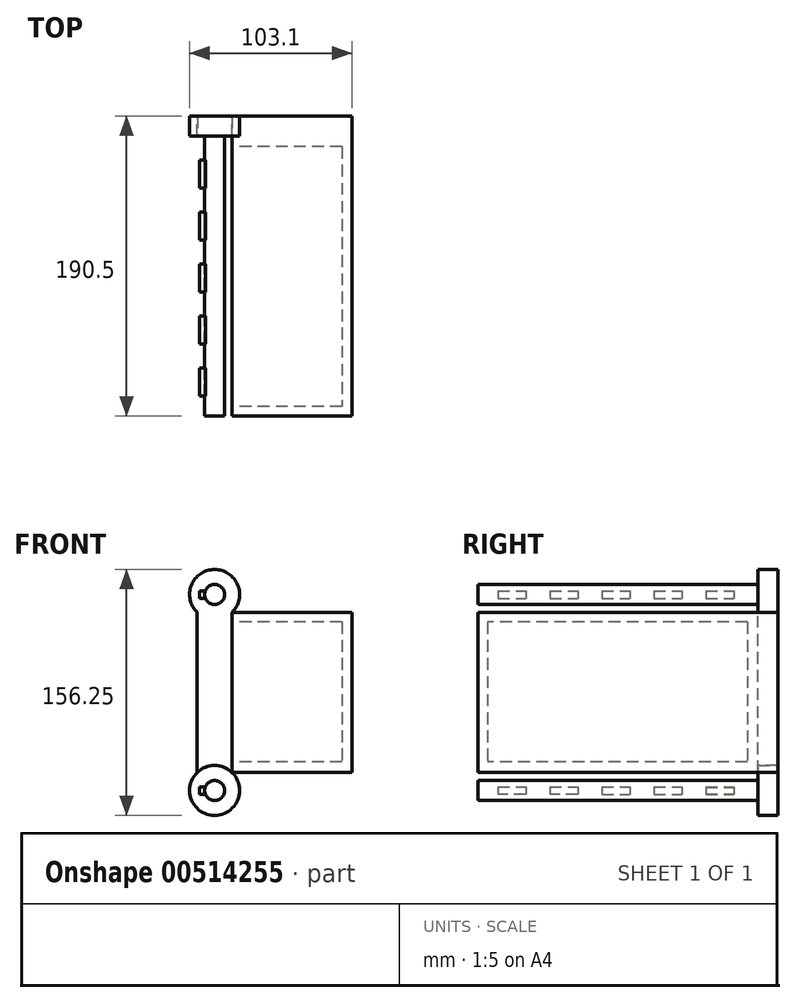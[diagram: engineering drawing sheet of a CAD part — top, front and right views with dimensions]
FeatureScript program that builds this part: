
annotation { "Feature Type Name" : "Feature", "Feature Type Description" : "" }
export const myFeature = defineFeature(function(context is Context, id is Id, definition is map)
    precondition{}
    {
        {
            var Q0;
            Q0=qCreatedBy(makeId("Front.planeOp"),FACE);
            var sketch = newSketch(context, id + "F0", { "sketchPlane" : qUnion([Q0])});
            skCircle(sketch, "E0", {"center": v(0, 0) * mm, "radius": 6.35 * mm});
            skSolve(sketch);
        }
        {
            var Q0;
            Q0=makeQuery(id+"F0.imprint","IMPRINT",FACE,{"disambiguationData":[TD([[makeQuery(id+"F0.imprint","IMPRINT",EDGE,{"derivedFrom":sQuery(id+"F0.wireOp",EDGE,"E0")}),1.0]])]});
            extrude(context, id + "F1", {"entities" : qUnion([Q0]), "depth" : 177.8 * mm, "offsetDistance" : 25.4 * mm});
        }
        {
            var Q0;
            Q0=makeQuery(id+"F1.opExtrude","CAP_FACE",FACE,{"disambiguationData":[OSD([sQuery(id+"F0.wireOp",EDGE,"E0")])],"isStart":true});
            var sketch = newSketch(context, id + "F2", { "sketchPlane" : qUnion([Q0])});
            skCircle(sketch, "E1", {"center": v(0, 0) * mm, "radius": 15.88 * mm});
            skSolve(sketch);
        }
        {
            var Q0;
            Q0=makeQuery(id+"F2.imprint","IMPRINT",FACE,{"disambiguationData":[TD([[makeQuery(id+"F2.imprint","IMPRINT",EDGE,{"derivedFrom":sQuery(id+"F2.wireOp",EDGE,"E1")}),1.0]])]});
            var Q1;
            Q1=makeQuery(id+"F2.imprint","IMPRINT",FACE,{"disambiguationData":[TD([[makeQuery(id+"F2.imprint","IMPRINT",EDGE,{"derivedFrom":makeQuery(id+"F1.opExtrude","CAP_EDGE",EDGE,{"disambiguationData":[OSD([sQuery(id+"F0.wireOp",EDGE,"E0")])],"isStart":true})}),-1.0]])]});
            extrude(context, id + "F3", {"entities" : qUnion([Q0, Q1]), "operationType" : NewBodyOperationType.ADD, "depth" : 12.7 * mm});
        }
        {
            var Q0;
            Q0=makeQuery(id+"F3.opExtrude","CAP_FACE",FACE,{"disambiguationData":[OSD([sQuery(id+"F2.wireOp",EDGE,"E1")])],"isStart":false});
            var sketch = newSketch(context, id + "F4", { "sketchPlane" : qUnion([Q0])});
            skArc(sketch, "E2", {"start": v(11, 11.44) * mm, "mid": v(0, 15.9) * mm, "end": v(-11.02, 11.43) * mm});
            skPoint(sketch, "E3.bottom.start.orphan", {"position": v(-15.88, 0) * mm});
            skLineSegment(sketch, "E4.bottom", {"start": v(-11.02, 11.43) * mm, "end": v(11, 11.43) * mm});
            skLineSegment(sketch, "E4.top", {"start": v(-11.02, 113.03) * mm, "end": v(11, 113.03) * mm});
            skLineSegment(sketch, "E4.left", {"start": v(-11.02, 11.43) * mm, "end": v(-11.02, 113.03) * mm});
            skLineSegment(sketch, "E4.right", {"start": v(11, 11.43) * mm, "end": v(11, 113.03) * mm});
            skLineSegment(sketch, "E5", {"start": v(0, 15.87) * mm, "end": v(0, 11.43) * mm});
            skPoint(sketch, "E5.startSnap0", {"position": v(0, 15.9) * mm});
            skPoint(sketch, "E5.endSnap0", {"position": v(0, 11.43) * mm});
            skSolve(sketch);
        }
        {
            var Q0;
            Q0=qCreatedBy(makeId("Front.planeOp"),FACE);
            var sketch = newSketch(context, id + "F5", { "sketchPlane" : qUnion([Q0])});
            skCircle(sketch, "E6", {"center": v(0, 124.5) * mm, "radius": 15.88 * mm});
            skSolve(sketch);
        }
        {
            var Q0;
            {var subQ0=sQuery(id+"F4.wireOp",EDGE,"E2");Q0=makeQuery(id+"F4.imprint","IMPRINT",FACE,{"disambiguationData":[TD([[makeQuery(id+"F4.imprint","IMPRINT",EDGE,{"derivedFrom":subQ0}),-1.0]])]});}
            extrude(context, id + "F6", {"entities" : qUnion([Q0]), "oppositeDirection" : true, "depth" : 12.7 * mm, "offsetDistance" : 25.4 * mm});
        }
        {
            var Q0;
            Q0=makeQuery(id+"F5.imprint","IMPRINT",FACE,{"disambiguationData":[TD([[makeQuery(id+"F5.imprint","IMPRINT",EDGE,{"derivedFrom":sQuery(id+"F5.wireOp",EDGE,"E6")}),1.0]])]});
            extrude(context, id + "F7", {"entities" : qUnion([Q0]), "operationType" : NewBodyOperationType.ADD, "oppositeDirection" : true, "depth" : 12.7 * mm, "offsetDistance" : 25.4 * mm});
        }
        {
            var Q0;
            Q0=makeQuery(id+"F7.boolean.opBoolean","MERGE",FACE,{"derivedFrom":[makeQuery(id+"F6.opExtrude","CAP_FACE",FACE,{"disambiguationData":[OSD([sQuery(id+"F4.wireOp",EDGE,"E2"),sQuery(id+"F4.wireOp",EDGE,"E4.top"),sQuery(id+"F4.wireOp",EDGE,"E4.left"),sQuery(id+"F4.wireOp",EDGE,"E4.right")])],"isStart":false}),makeQuery(id+"F7.opExtrude","CAP_FACE",FACE,{"disambiguationData":[OSD([sQuery(id+"F5.wireOp",EDGE,"E6")])],"isStart":true})]});
            var sketch = newSketch(context, id + "F8", { "sketchPlane" : qUnion([Q0])});
            skCircle(sketch, "E7", {"center": v(0, 124.5) * mm, "radius": 6.35 * mm});
            skSolve(sketch);
        }
        {
            var Q0;
            Q0=makeQuery(id+"F8.imprint","IMPRINT",FACE,{"disambiguationData":[TD([[makeQuery(id+"F8.imprint","IMPRINT",EDGE,{"derivedFrom":sQuery(id+"F8.wireOp",EDGE,"E7")}),1.0]])]});
            extrude(context, id + "F9", {"entities" : qUnion([Q0]), "operationType" : NewBodyOperationType.ADD, "depth" : 177.8 * mm, "offsetDistance" : 25.4 * mm});
        }
        {
            var Q0;
            Q0=makeQuery(id+"F7.boolean.opBoolean","MERGE",FACE,{"derivedFrom":[makeQuery(id+"F6.opExtrude","CAP_FACE",FACE,{"disambiguationData":[OSD([sQuery(id+"F4.wireOp",EDGE,"E2"),sQuery(id+"F4.wireOp",EDGE,"E4.top"),sQuery(id+"F4.wireOp",EDGE,"E4.left"),sQuery(id+"F4.wireOp",EDGE,"E4.right")])],"isStart":false}),makeQuery(id+"F7.opExtrude","CAP_FACE",FACE,{"disambiguationData":[OSD([sQuery(id+"F5.wireOp",EDGE,"E6")])],"isStart":true})]});
            var sketch = newSketch(context, id + "F10", { "sketchPlane" : qUnion([Q0])});
            skLineSegment(sketch, "E8.bottom", {"start": v(11.02, 113.03) * mm, "end": v(87.22, 113.03) * mm});
            skLineSegment(sketch, "E8.top", {"start": v(11.02, 11.43) * mm, "end": v(87.22, 11.43) * mm});
            skLineSegment(sketch, "E8.left", {"start": v(11.02, 113.03) * mm, "end": v(11.02, 11.43) * mm});
            skLineSegment(sketch, "E8.right", {"start": v(87.22, 113.03) * mm, "end": v(87.22, 11.43) * mm});
            skSolve(sketch);
        }
        {
            var Q0;
            Q0=makeQuery(id+"F10.imprint","IMPRINT",FACE,{"disambiguationData":[TD([[makeQuery(id+"F10.imprint","IMPRINT",EDGE,{"derivedFrom":sQuery(id+"F10.wireOp",EDGE,"E8.bottom")}),-1.0]])]});
            extrude(context, id + "F11", {"entities" : qUnion([Q0]), "operationType" : NewBodyOperationType.ADD, "depth" : 177.8 * mm, "offsetDistance" : 25.4 * mm, "hasSecondDirection" : true, "secondDirectionOppositeDirection" : true, "secondDirectionDepth" : 12.7 * mm});
        }
        {
            var Q0;
            Q0=makeQuery(id+"F11.opExtrude","SWEPT_FACE",FACE,{"disambiguationData":[OSD([sQuery(id+"F10.wireOp",EDGE,"E8.left")])]});
            var sketch = newSketch(context, id + "F12", { "sketchPlane" : qUnion([Q0])});
            skLineSegment(sketch, "E9.bottom", {"start": v(6.74, 107.06) * mm, "end": v(171.84, 107.06) * mm});
            skLineSegment(sketch, "E9.top", {"start": v(6.74, 18.16) * mm, "end": v(171.84, 18.16) * mm});
            skLineSegment(sketch, "E9.left", {"start": v(6.74, 107.06) * mm, "end": v(6.74, 18.16) * mm});
            skLineSegment(sketch, "E9.right", {"start": v(171.84, 107.06) * mm, "end": v(171.84, 18.16) * mm});
            skSolve(sketch);
        }
        {
            var Q0;
            Q0=makeQuery(id+"F12.imprint","IMPRINT",FACE,{"disambiguationData":[TD([[makeQuery(id+"F12.imprint","IMPRINT",EDGE,{"derivedFrom":sQuery(id+"F12.wireOp",EDGE,"E9.bottom")}),-1.0]])]});
            extrude(context, id + "F13", {"entities" : qUnion([Q0]), "operationType" : NewBodyOperationType.REMOVE, "oppositeDirection" : true, "depth" : 69.85 * mm, "offsetDistance" : 25.4 * mm});
        }
        {
            var Q0;
            Q0=makeQuery(id+"F3.opExtrude","CAP_FACE",FACE,{"disambiguationData":[OSD([sQuery(id+"F2.wireOp",EDGE,"E1")])],"isStart":true});
            var sketch = newSketch(context, id + "F14", { "sketchPlane" : qUnion([Q0])});
            skArc(sketch, "E10", {"start": v(-5.87, 2.41) * mm, "mid": v(-6.36, -0.03) * mm, "end": v(-5.85, -2.46) * mm});
            skLineSegment(sketch, "E11", {"start": v(-5.85, -2.46) * mm, "end": v(-9.66, -2.46) * mm});
            skLineSegment(sketch, "E12", {"start": v(-5.87, 2.41) * mm, "end": v(-9.68, 2.41) * mm});
            skLineSegment(sketch, "E13", {"start": v(-9.68, 2.41) * mm, "end": v(-9.66, -2.46) * mm});
            skSolve(sketch);
        }
        {
            var Q0;
            {var subQ0=sQuery(id+"F14.wireOp",EDGE,"E13");Q0=makeQuery(id+"F14.imprint","IMPRINT",FACE,{"disambiguationData":[TD([[makeQuery(id+"F14.imprint","IMPRINT",EDGE,{"derivedFrom":subQ0}),1.0]])]});}
            extrude(context, id + "F15", {"entities" : qUnion([Q0]), "operationType" : NewBodyOperationType.ADD, "depth" : 33.02 * mm, "offsetDistance" : 25.4 * mm, "hasSecondDirection" : true, "secondDirectionOppositeDirection" : false, "secondDirectionDepth" : 15.24 * mm});
        }
        {
            var Q0;
            Q0=makeQuery(id+"F15.opExtrude","CAP_FACE",FACE,{"disambiguationData":[OSD([sQuery(id+"F0.wireOp",EDGE,"E0"),sQuery(id+"F14.wireOp",EDGE,"E10"),sQuery(id+"F14.wireOp",EDGE,"E11"),sQuery(id+"F14.wireOp",EDGE,"E12"),sQuery(id+"F14.wireOp",EDGE,"E13")])],"isStart":false});
            var sketch = newSketch(context, id + "F16", { "sketchPlane" : qUnion([Q0])});
            skArc(sketch, "E14", {"start": v(-5.95, 2.41) * mm, "mid": v(-6.44, -0.02) * mm, "end": v(-5.93, -2.46) * mm});
            skLineSegment(sketch, "E15", {"start": v(-5.93, -2.46) * mm, "end": v(-9.74, -2.46) * mm});
            skLineSegment(sketch, "E16", {"start": v(-5.95, 2.41) * mm, "end": v(-9.76, 2.41) * mm});
            skLineSegment(sketch, "E17", {"start": v(-9.76, 2.41) * mm, "end": v(-9.74, -2.46) * mm});
            skSolve(sketch);
        }
        {
            var Q0;
            {var subQ0=sQuery(id+"F16.wireOp",EDGE,"E15");var subQ1=sQuery(id+"F16.wireOp",EDGE,"E14");var subQ2=makeQuery(id+"F16.imprint","INTERSECT",VERTEX,{"derivedFrom":[subQ1,subQ0]});Q0=makeQuery(id+"F16.imprint","IMPRINT",FACE,{"disambiguationData":[TD([[makeQuery(id+"F16.imprint","IMPRINT",EDGE,{"disambiguationData":[TD([[subQ2,1.0]])],"derivedFrom":subQ1}),-1.0]])]});}
            var Q1;
            Q1=sQuery(id+"F16.wireOp",EDGE,"E14");
            var Q2;
            Q2=sQuery(id+"F16.wireOp",EDGE,"E15");
            var Q3;
            Q3=sQuery(id+"F16.wireOp",EDGE,"E16");
            var Q4;
            Q4=sQuery(id+"F16.wireOp",EDGE,"E17");
            extrude(context, id + "F17", {"entities" : qUnion([Q0]), "surfaceEntities" : qUnion([Q1, Q2, Q3, Q4]), "depth" : 33.02 * mm, "offsetDistance" : 25.4 * mm, "hasSecondDirection" : true, "secondDirectionOppositeDirection" : false, "secondDirectionDepth" : 15.24 * mm});
        }
        {
            var Q0;
            Q0=makeQuery(id+"F17.opExtrude","CAP_FACE",FACE,{"disambiguationData":[OSD([sQuery(id+"F14.wireOp",EDGE,"E12"),sQuery(id+"F14.wireOp",EDGE,"E13"),sQuery(id+"F16.wireOp",EDGE,"E14"),sQuery(id+"F16.wireOp",EDGE,"E15")])],"isStart":false});
            var sketch = newSketch(context, id + "F18", { "sketchPlane" : qUnion([Q0])});
            skArc(sketch, "E18", {"start": v(-6, 2.41) * mm, "mid": v(-6.48, -0.02) * mm, "end": v(-5.97, -2.46) * mm});
            skLineSegment(sketch, "E19", {"start": v(-5.97, -2.46) * mm, "end": v(-9.78, -2.46) * mm});
            skLineSegment(sketch, "E20", {"start": v(-6, 2.41) * mm, "end": v(-9.8, 2.41) * mm});
            skLineSegment(sketch, "E21", {"start": v(-9.8, 2.41) * mm, "end": v(-9.78, -2.46) * mm});
            skSolve(sketch);
        }
        {
            var Q0;
            {var subQ0=sQuery(id+"F18.wireOp",EDGE,"E19");var subQ1=sQuery(id+"F18.wireOp",EDGE,"E18");var subQ2=makeQuery(id+"F18.imprint","INTERSECT",VERTEX,{"derivedFrom":[subQ1,subQ0]});Q0=makeQuery(id+"F18.imprint","IMPRINT",FACE,{"disambiguationData":[TD([[makeQuery(id+"F18.imprint","IMPRINT",EDGE,{"disambiguationData":[TD([[subQ2,1.0]])],"derivedFrom":subQ1}),-1.0]])]});}
            var Q1;
            Q1=sQuery(id+"F18.wireOp",EDGE,"E18");
            var Q2;
            Q2=sQuery(id+"F18.wireOp",EDGE,"E19");
            var Q3;
            Q3=sQuery(id+"F18.wireOp",EDGE,"E20");
            var Q4;
            Q4=sQuery(id+"F18.wireOp",EDGE,"E21");
            extrude(context, id + "F19", {"entities" : qUnion([Q0]), "surfaceEntities" : qUnion([Q1, Q2, Q3, Q4]), "depth" : 33.02 * mm, "offsetDistance" : 25.4 * mm, "hasSecondDirection" : true, "secondDirectionOppositeDirection" : false, "secondDirectionDepth" : 15.24 * mm});
        }
        {
            var Q0;
            Q0=makeQuery(id+"F19.opExtrude","CAP_FACE",FACE,{"disambiguationData":[OSD([sQuery(id+"F14.wireOp",EDGE,"E12"),sQuery(id+"F14.wireOp",EDGE,"E13"),sQuery(id+"F18.wireOp",EDGE,"E18"),sQuery(id+"F18.wireOp",EDGE,"E19")])],"isStart":false});
            var sketch = newSketch(context, id + "F20", { "sketchPlane" : qUnion([Q0])});
            skArc(sketch, "E22", {"start": v(-6.01, 2.41) * mm, "mid": v(-6.5, -0.02) * mm, "end": v(-6, -2.46) * mm});
            skLineSegment(sketch, "E23", {"start": v(-6, -2.46) * mm, "end": v(-9.8, -2.46) * mm});
            skLineSegment(sketch, "E24", {"start": v(-6.01, 2.41) * mm, "end": v(-9.82, 2.41) * mm});
            skLineSegment(sketch, "E25", {"start": v(-9.82, 2.41) * mm, "end": v(-9.8, -2.46) * mm});
            skSolve(sketch);
        }
        {
            var Q0;
            {var subQ5=makeQuery(id+"F19.opExtrude","CAP_EDGE",EDGE,{"disambiguationData":[OSD([sQuery(id+"F14.wireOp",EDGE,"E13")])],"isStart":false});Q0=makeQuery(id+"F20.imprint","IMPRINT",FACE,{"disambiguationData":[TD([[makeQuery(id+"F20.imprint","IMPRINT",EDGE,{"derivedFrom":subQ5}),1.0]])]});}
            var Q1;
            Q1=sQuery(id+"F20.wireOp",EDGE,"E22");
            var Q2;
            Q2=sQuery(id+"F20.wireOp",EDGE,"E23");
            var Q3;
            Q3=sQuery(id+"F20.wireOp",EDGE,"E24");
            var Q4;
            Q4=sQuery(id+"F20.wireOp",EDGE,"E25");
            extrude(context, id + "F21", {"entities" : qUnion([Q0]), "surfaceEntities" : qUnion([Q1, Q2, Q3, Q4]), "depth" : 33.02 * mm, "offsetDistance" : 25.4 * mm, "hasSecondDirection" : true, "secondDirectionOppositeDirection" : false, "secondDirectionDepth" : 15.24 * mm});
        }
        {
            var Q0;
            Q0=makeQuery(id+"F21.opExtrude","CAP_FACE",FACE,{"disambiguationData":[OSD([sQuery(id+"F14.wireOp",EDGE,"E12"),sQuery(id+"F14.wireOp",EDGE,"E13"),sQuery(id+"F20.wireOp",EDGE,"E22"),sQuery(id+"F20.wireOp",EDGE,"E23")])],"isStart":false});
            var sketch = newSketch(context, id + "F22", { "sketchPlane" : qUnion([Q0])});
            skArc(sketch, "E26", {"start": v(-6.02, 2.41) * mm, "mid": v(-6.5, -0.02) * mm, "end": v(-6, -2.46) * mm});
            skLineSegment(sketch, "E27", {"start": v(-6, -2.46) * mm, "end": v(-9.81, -2.46) * mm});
            skLineSegment(sketch, "E28", {"start": v(-6.02, 2.41) * mm, "end": v(-9.83, 2.41) * mm});
            skLineSegment(sketch, "E29", {"start": v(-9.83, 2.41) * mm, "end": v(-9.81, -2.46) * mm});
            skSolve(sketch);
        }
        {
            var Q0;
            {var subQ5=makeQuery(id+"F21.opExtrude","CAP_EDGE",EDGE,{"disambiguationData":[OSD([sQuery(id+"F14.wireOp",EDGE,"E13")])],"isStart":false});Q0=makeQuery(id+"F22.imprint","IMPRINT",FACE,{"disambiguationData":[TD([[makeQuery(id+"F22.imprint","IMPRINT",EDGE,{"derivedFrom":subQ5}),1.0]])]});}
            var Q1;
            Q1=sQuery(id+"F22.wireOp",EDGE,"E26");
            var Q2;
            Q2=sQuery(id+"F22.wireOp",EDGE,"E27");
            var Q3;
            Q3=sQuery(id+"F22.wireOp",EDGE,"E28");
            var Q4;
            Q4=sQuery(id+"F22.wireOp",EDGE,"E29");
            extrude(context, id + "F23", {"entities" : qUnion([Q0]), "surfaceEntities" : qUnion([Q1, Q2, Q3, Q4]), "depth" : 33.02 * mm, "offsetDistance" : 25.4 * mm, "hasSecondDirection" : true, "secondDirectionOppositeDirection" : false, "secondDirectionDepth" : 15.24 * mm});
        }
        {
            var Q0;
            Q0=makeQuery(id+"F7.boolean.opBoolean","MERGE",FACE,{"derivedFrom":[makeQuery(id+"F6.opExtrude","CAP_FACE",FACE,{"disambiguationData":[OSD([sQuery(id+"F4.wireOp",EDGE,"E2"),sQuery(id+"F4.wireOp",EDGE,"E4.top"),sQuery(id+"F4.wireOp",EDGE,"E4.left"),sQuery(id+"F4.wireOp",EDGE,"E4.right")])],"isStart":false}),makeQuery(id+"F7.opExtrude","CAP_FACE",FACE,{"disambiguationData":[OSD([sQuery(id+"F5.wireOp",EDGE,"E6")])],"isStart":true})]});
            var sketch = newSketch(context, id + "F24", { "sketchPlane" : qUnion([Q0])});
            skArc(sketch, "E30", {"start": v(-5.9, 126.87) * mm, "mid": v(-6.38, 124.43) * mm, "end": v(-5.88, 122) * mm});
            skLineSegment(sketch, "E31", {"start": v(-5.88, 122) * mm, "end": v(-9.69, 122) * mm});
            skLineSegment(sketch, "E32", {"start": v(-5.9, 126.87) * mm, "end": v(-9.7, 126.87) * mm});
            skLineSegment(sketch, "E33", {"start": v(-9.7, 126.87) * mm, "end": v(-9.69, 122) * mm});
            skSolve(sketch);
        }
        {
            var Q0;
            Q0=makeQuery(id+"F24.imprint","IMPRINT",FACE,{"disambiguationData":[TD([[makeQuery(id+"F24.imprint","IMPRINT",EDGE,{"derivedFrom":sQuery(id+"F24.wireOp",EDGE,"E30")}),-1.0]])]});
            extrude(context, id + "F25", {"entities" : qUnion([Q0]), "depth" : 33.02 * mm, "offsetDistance" : 25.4 * mm, "hasSecondDirection" : true, "secondDirectionOppositeDirection" : false, "secondDirectionDepth" : 15.24 * mm});
        }
        {
            var Q0;
            Q0=makeQuery(id+"F25.opExtrude","CAP_FACE",FACE,{"disambiguationData":[OSD([sQuery(id+"F24.wireOp",EDGE,"E30"),sQuery(id+"F24.wireOp",EDGE,"E31"),sQuery(id+"F24.wireOp",EDGE,"E32"),sQuery(id+"F24.wireOp",EDGE,"E33")])],"isStart":false});
            extrude(context, id + "F26", {"entities" : qUnion([Q0]), "depth" : 33.02 * mm, "offsetDistance" : 25.4 * mm, "hasSecondDirection" : true, "secondDirectionOppositeDirection" : false, "secondDirectionDepth" : 15.24 * mm});
        }
        {
            var Q0;
            Q0=makeQuery(id+"F26.opExtrude","CAP_FACE",FACE,{"disambiguationData":[OSD([sQuery(id+"F24.wireOp",EDGE,"E30"),sQuery(id+"F24.wireOp",EDGE,"E31"),sQuery(id+"F24.wireOp",EDGE,"E32"),sQuery(id+"F24.wireOp",EDGE,"E33")])],"isStart":false});
            extrude(context, id + "F27", {"entities" : qUnion([Q0]), "depth" : 33.02 * mm, "offsetDistance" : 25.4 * mm, "hasSecondDirection" : true, "secondDirectionOppositeDirection" : false, "secondDirectionDepth" : 15.24 * mm});
        }
        {
            var Q0;
            Q0=makeQuery(id+"F27.opExtrude","CAP_FACE",FACE,{"disambiguationData":[OSD([sQuery(id+"F24.wireOp",EDGE,"E30"),sQuery(id+"F24.wireOp",EDGE,"E31"),sQuery(id+"F24.wireOp",EDGE,"E32"),sQuery(id+"F24.wireOp",EDGE,"E33")])],"isStart":false});
            extrude(context, id + "F28", {"entities" : qUnion([Q0]), "depth" : 33.02 * mm, "offsetDistance" : 25.4 * mm, "hasSecondDirection" : true, "secondDirectionOppositeDirection" : false, "secondDirectionDepth" : 15.24 * mm});
        }
        {
            var Q0;
            Q0=makeQuery(id+"F28.opExtrude","CAP_FACE",FACE,{"disambiguationData":[OSD([sQuery(id+"F24.wireOp",EDGE,"E30"),sQuery(id+"F24.wireOp",EDGE,"E31"),sQuery(id+"F24.wireOp",EDGE,"E32"),sQuery(id+"F24.wireOp",EDGE,"E33")])],"isStart":false});
            extrude(context, id + "F29", {"entities" : qUnion([Q0]), "depth" : 33.02 * mm, "offsetDistance" : 25.4 * mm, "hasSecondDirection" : true, "secondDirectionOppositeDirection" : false, "secondDirectionDepth" : 15.24 * mm});
        }
    });
